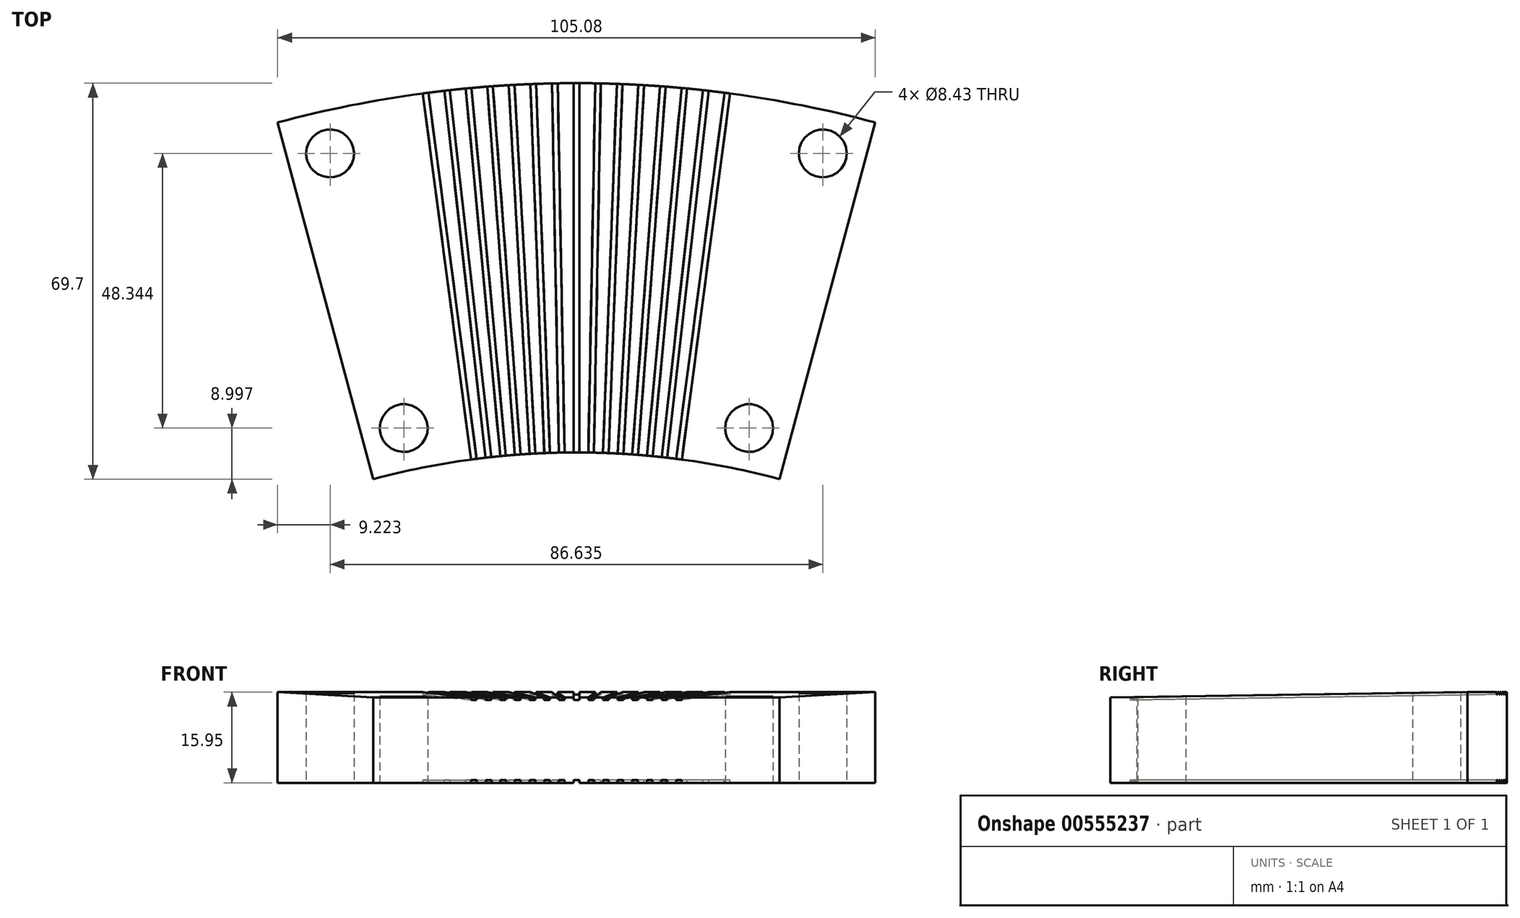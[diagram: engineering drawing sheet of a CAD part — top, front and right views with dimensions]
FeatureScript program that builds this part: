
annotation { "Feature Type Name" : "Feature", "Feature Type Description" : "" }
export const myFeature = defineFeature(function(context is Context, id is Id, definition is map)
    precondition{}
    {
        {
            var Q0;
            Q0=qCreatedBy(makeId("Right.planeOp"),FACE);
            var sketch = newSketch(context, id + "F0", { "sketchPlane" : qUnion([Q0])});
            skLineSegment(sketch, "E0", {"start": v(0, 0) * mm, "end": v(0, 15) * mm});
            skLineSegment(sketch, "E1", {"start": v(0, 15) * mm, "end": v(65, 15.95) * mm});
            skLineSegment(sketch, "E2", {"start": v(65, 15.95) * mm, "end": v(65, 0) * mm});
            skLineSegment(sketch, "E3", {"start": v(65, 0) * mm, "end": v(0, 0) * mm});
            skLineSegment(sketch, "E4", {"start": v(-138, 37.06) * mm, "end": v(-138, 5.42) * mm});
            skSolve(sketch);
        }
        {
            var Q0;
            Q0=makeQuery(id+"F0.imprint","IMPRINT",FACE,{"disambiguationData":[TD([[makeQuery(id+"F0.imprint","IMPRINT",EDGE,{"derivedFrom":sQuery(id+"F0.wireOp",EDGE,"E0")}),-1.0]])]});
            var Q1;
            Q1=sQuery(id+"F0.wireOp",EDGE,"E4");
            revolve(context, id + "F1", {"entities" : qUnion([Q0]), "axis" : qUnion([Q1]), "revolveType" : RevolveType.SYMMETRIC, "angle" : 30 * degree});
        }
        {
            var Q0;
            Q0=qCreatedBy(makeId("Top.planeOp"),FACE);
            var sketch = newSketch(context, id + "F2", { "sketchPlane" : qUnion([Q0])});
            skLineSegment(sketch, "E5", {"start": v(0, -138) * mm, "end": v(-26.5, 63.26) * mm});
            skLineSegment(sketch, "E6", {"start": v(0, -138) * mm, "end": v(26.5, 63.26) * mm});
            skLineSegment(sketch, "E7.1.0", {"start": v(0, -138) * mm, "end": v(-22.73, 63.72) * mm});
            skLineSegment(sketch, "E7.2.0", {"start": v(0, -138) * mm, "end": v(-18.95, 64.11) * mm});
            skLineSegment(sketch, "E7.3.0", {"start": v(0, -138) * mm, "end": v(-15.17, 64.43) * mm});
            skLineSegment(sketch, "E7.4.0", {"start": v(0, -138) * mm, "end": v(-11.38, 64.68) * mm});
            skLineSegment(sketch, "E7.5.0", {"start": v(0, -138) * mm, "end": v(-7.6, 64.86) * mm});
            skLineSegment(sketch, "E7.6.0", {"start": v(0, -138) * mm, "end": v(-3.8, 64.96) * mm});
            skLineSegment(sketch, "E7.7.0", {"start": v(0, -138) * mm, "end": v(0, 65) * mm});
            skLineSegment(sketch, "E7.8.0", {"start": v(0, -138) * mm, "end": v(3.8, 64.96) * mm});
            skLineSegment(sketch, "E7.9.0", {"start": v(0, -138) * mm, "end": v(7.6, 64.86) * mm});
            skLineSegment(sketch, "E7.10.0", {"start": v(0, -138) * mm, "end": v(11.38, 64.68) * mm});
            skLineSegment(sketch, "E7.11.0", {"start": v(0, -138) * mm, "end": v(15.17, 64.43) * mm});
            skLineSegment(sketch, "E7.12.0", {"start": v(0, -138) * mm, "end": v(18.95, 64.11) * mm});
            skLineSegment(sketch, "E7.13.0", {"start": v(0, -138) * mm, "end": v(22.73, 63.72) * mm});
            skPoint(sketch, "E7.center", {"position": v(0, -138) * mm});
            skLineSegment(sketch, "E7.anchor1", {"start": v(0, -138) * mm, "end": v(-26.5, 63.26) * mm, "construction": true});
            skLineSegment(sketch, "E7.anchor2", {"start": v(0, -138) * mm, "end": v(26.5, 63.26) * mm, "construction": true});
            skLineSegment(sketch, "E8.bottom", {"start": v(43.3, 187.13) * mm, "end": v(42.32, 187.26) * mm});
            skLineSegment(sketch, "E8.top", {"start": v(10.68, -60.73) * mm, "end": v(9.69, -60.6) * mm});
            skLineSegment(sketch, "E8.left", {"start": v(43.3, 187.13) * mm, "end": v(10.68, -60.73) * mm});
            skLineSegment(sketch, "E8.right", {"start": v(42.32, 187.26) * mm, "end": v(9.69, -60.6) * mm});
            skPoint(sketch, "E8.middle", {"position": v(26.5, 63.26) * mm});
            skLineSegment(sketch, "E9.bottom", {"start": v(37.22, 187.88) * mm, "end": v(36.23, 188) * mm});
            skLineSegment(sketch, "E9.top", {"start": v(9.23, -60.55) * mm, "end": v(8.24, -60.43) * mm});
            skLineSegment(sketch, "E9.left", {"start": v(37.22, 187.88) * mm, "end": v(9.23, -60.55) * mm});
            skLineSegment(sketch, "E9.right", {"start": v(36.23, 188) * mm, "end": v(8.24, -60.43) * mm});
            skPoint(sketch, "E9.middle", {"position": v(22.73, 63.72) * mm});
            skLineSegment(sketch, "E10.bottom", {"start": v(31.12, 188.52) * mm, "end": v(30.13, 188.61) * mm});
            skLineSegment(sketch, "E10.top", {"start": v(7.78, -60.39) * mm, "end": v(6.78, -60.3) * mm});
            skLineSegment(sketch, "E10.left", {"start": v(31.12, 188.52) * mm, "end": v(7.78, -60.39) * mm});
            skLineSegment(sketch, "E10.right", {"start": v(30.13, 188.61) * mm, "end": v(6.78, -60.3) * mm});
            skPoint(sketch, "E10.middle", {"position": v(18.95, 64.11) * mm});
            skLineSegment(sketch, "E11.bottom", {"start": v(25.01, 189.05) * mm, "end": v(24.01, 189.12) * mm});
            skLineSegment(sketch, "E11.top", {"start": v(6.33, -60.26) * mm, "end": v(5.33, -60.18) * mm});
            skLineSegment(sketch, "E11.left", {"start": v(25.01, 189.05) * mm, "end": v(6.33, -60.26) * mm});
            skLineSegment(sketch, "E11.right", {"start": v(24.01, 189.12) * mm, "end": v(5.33, -60.18) * mm});
            skPoint(sketch, "E11.middle", {"position": v(15.17, 64.43) * mm});
            skLineSegment(sketch, "E12.bottom", {"start": v(18.9, 189.46) * mm, "end": v(17.9, 189.51) * mm});
            skLineSegment(sketch, "E12.top", {"start": v(4.87, -60.15) * mm, "end": v(3.87, -60.1) * mm});
            skLineSegment(sketch, "E12.left", {"start": v(18.9, 189.46) * mm, "end": v(4.87, -60.15) * mm});
            skLineSegment(sketch, "E12.right", {"start": v(17.9, 189.51) * mm, "end": v(3.87, -60.1) * mm});
            skPoint(sketch, "E12.middle", {"position": v(11.38, 64.68) * mm});
            skLineSegment(sketch, "E13.bottom", {"start": v(6.63, 189.93) * mm, "end": v(5.63, 189.95) * mm});
            skLineSegment(sketch, "E13.top", {"start": v(1.96, -60.02) * mm, "end": v(0.96, -60) * mm});
            skLineSegment(sketch, "E13.left", {"start": v(6.63, 189.93) * mm, "end": v(1.96, -60.02) * mm});
            skLineSegment(sketch, "E13.right", {"start": v(5.63, 189.95) * mm, "end": v(0.96, -60) * mm});
            skPoint(sketch, "E13.middle", {"position": v(3.8, 64.96) * mm});
            skLineSegment(sketch, "E14.bottom", {"start": v(0.5, 190) * mm, "end": v(-0.5, 190) * mm});
            skLineSegment(sketch, "E14.top", {"start": v(0.5, -60) * mm, "end": v(-0.5, -60) * mm});
            skLineSegment(sketch, "E14.left", {"start": v(0.5, 190) * mm, "end": v(0.5, -60) * mm});
            skLineSegment(sketch, "E14.right", {"start": v(-0.5, 190) * mm, "end": v(-0.5, -60) * mm});
            skPoint(sketch, "E14.middle", {"position": v(0, 65) * mm});
            skLineSegment(sketch, "E15.bottom", {"start": v(12.76, 189.75) * mm, "end": v(11.76, 189.79) * mm});
            skLineSegment(sketch, "E15.top", {"start": v(3.42, -60.07) * mm, "end": v(2.42, -60.04) * mm});
            skLineSegment(sketch, "E15.left", {"start": v(12.76, 189.75) * mm, "end": v(3.42, -60.07) * mm});
            skLineSegment(sketch, "E15.right", {"start": v(11.76, 189.79) * mm, "end": v(2.42, -60.04) * mm});
            skPoint(sketch, "E15.middle", {"position": v(7.6, 64.86) * mm});
            skLineSegment(sketch, "E16.bottom", {"start": v(-5.63, 189.95) * mm, "end": v(-6.63, 189.93) * mm});
            skLineSegment(sketch, "E16.top", {"start": v(-0.96, -60) * mm, "end": v(-1.96, -60.02) * mm});
            skLineSegment(sketch, "E16.left", {"start": v(-5.63, 189.95) * mm, "end": v(-0.96, -60) * mm});
            skLineSegment(sketch, "E16.right", {"start": v(-6.63, 189.93) * mm, "end": v(-1.96, -60.02) * mm});
            skPoint(sketch, "E16.middle", {"position": v(-3.8, 64.96) * mm});
            skLineSegment(sketch, "E17.bottom", {"start": v(-30.13, 188.61) * mm, "end": v(-31.12, 188.52) * mm});
            skLineSegment(sketch, "E17.top", {"start": v(-6.78, -60.3) * mm, "end": v(-7.78, -60.39) * mm});
            skLineSegment(sketch, "E17.left", {"start": v(-30.13, 188.61) * mm, "end": v(-6.78, -60.3) * mm});
            skLineSegment(sketch, "E17.right", {"start": v(-31.12, 188.52) * mm, "end": v(-7.78, -60.39) * mm});
            skPoint(sketch, "E17.middle", {"position": v(-18.95, 64.11) * mm});
            skLineSegment(sketch, "E18.bottom", {"start": v(-36.23, 188) * mm, "end": v(-37.22, 187.88) * mm});
            skLineSegment(sketch, "E18.top", {"start": v(-8.24, -60.43) * mm, "end": v(-9.23, -60.55) * mm});
            skLineSegment(sketch, "E18.left", {"start": v(-36.23, 188) * mm, "end": v(-8.24, -60.43) * mm});
            skLineSegment(sketch, "E18.right", {"start": v(-37.22, 187.88) * mm, "end": v(-9.23, -60.55) * mm});
            skPoint(sketch, "E18.middle", {"position": v(-22.73, 63.72) * mm});
            skLineSegment(sketch, "E19.bottom", {"start": v(-42.32, 187.26) * mm, "end": v(-43.3, 187.13) * mm});
            skLineSegment(sketch, "E19.top", {"start": v(-9.69, -60.6) * mm, "end": v(-10.68, -60.73) * mm});
            skLineSegment(sketch, "E19.left", {"start": v(-42.32, 187.26) * mm, "end": v(-9.69, -60.6) * mm});
            skLineSegment(sketch, "E19.right", {"start": v(-43.3, 187.13) * mm, "end": v(-10.68, -60.73) * mm});
            skPoint(sketch, "E19.middle", {"position": v(-26.5, 63.26) * mm});
            skLineSegment(sketch, "E20.bottom", {"start": v(-24.01, 189.12) * mm, "end": v(-25.01, 189.05) * mm});
            skLineSegment(sketch, "E20.top", {"start": v(-5.33, -60.18) * mm, "end": v(-6.33, -60.26) * mm});
            skLineSegment(sketch, "E20.left", {"start": v(-24.01, 189.12) * mm, "end": v(-5.33, -60.18) * mm});
            skLineSegment(sketch, "E20.right", {"start": v(-25.01, 189.05) * mm, "end": v(-6.33, -60.26) * mm});
            skPoint(sketch, "E20.middle", {"position": v(-15.17, 64.43) * mm});
            skLineSegment(sketch, "E21.bottom", {"start": v(-17.9, 189.51) * mm, "end": v(-18.9, 189.46) * mm});
            skLineSegment(sketch, "E21.top", {"start": v(-3.87, -60.1) * mm, "end": v(-4.87, -60.15) * mm});
            skLineSegment(sketch, "E21.left", {"start": v(-17.9, 189.51) * mm, "end": v(-3.87, -60.1) * mm});
            skLineSegment(sketch, "E21.right", {"start": v(-18.9, 189.46) * mm, "end": v(-4.87, -60.15) * mm});
            skPoint(sketch, "E21.middle", {"position": v(-11.38, 64.68) * mm});
            skLineSegment(sketch, "E22.bottom", {"start": v(-11.76, 189.79) * mm, "end": v(-12.76, 189.75) * mm});
            skLineSegment(sketch, "E22.top", {"start": v(-2.42, -60.04) * mm, "end": v(-3.42, -60.07) * mm});
            skLineSegment(sketch, "E22.left", {"start": v(-11.76, 189.79) * mm, "end": v(-2.42, -60.04) * mm});
            skLineSegment(sketch, "E22.right", {"start": v(-12.76, 189.75) * mm, "end": v(-3.42, -60.07) * mm});
            skPoint(sketch, "E22.middle", {"position": v(-7.6, 64.86) * mm});
            skSolve(sketch);
        }
        {
            var Q0;
            Q0 = qSketchRegion(id + "F2", true);
            extrude(context, id + "F3", {"entities" : qUnion([Q0]), "operationType" : NewBodyOperationType.REMOVE, "depth" : .5 * mm, "offsetDistance" : 25 * mm});
        }
        {
            var Q0;
            Q0=makeQuery(id+"F1.opRevolve","CAP_VERTEX",VERTEX,{"disambiguationData":[OSD([sQuery(id+"F0.wireOp",EDGE,"E1"),sQuery(id+"F0.wireOp",EDGE,"E2")])],"isStart":true});
            var Q1;
            Q1=makeQuery(id+"F1.opRevolve","CAP_VERTEX",VERTEX,{"disambiguationData":[OSD([sQuery(id+"F0.wireOp",EDGE,"E1"),sQuery(id+"F0.wireOp",EDGE,"E2")])],"isStart":false});
            var Q2;
            Q2=makeQuery(id+"F1.opRevolve","CAP_VERTEX",VERTEX,{"disambiguationData":[OSD([sQuery(id+"F0.wireOp",EDGE,"E0"),sQuery(id+"F0.wireOp",EDGE,"E1")])],"isStart":false});
            cPlane(context, id + "F4", {"entities" : qUnion([Q0, Q1, Q2]), "cplaneType" : CPlaneType.THREE_POINT, "offset" : 25 * mm, "width" : 150 * mm, "height" : 150 * mm});
        }
        {
            var Q0;
            Q0=qCreatedBy(id+"F4.planeOp",FACE);
            var sketch = newSketch(context, id + "F5", { "sketchPlane" : qUnion([Q0])});
            skLineSegment(sketch, "E23", {"start": v(0, -137.98) * mm, "end": v(-26.5, 63.28) * mm});
            skLineSegment(sketch, "E24", {"start": v(0, -137.98) * mm, "end": v(26.5, 63.28) * mm});
            skLineSegment(sketch, "E25.1.0", {"start": v(0, -137.98) * mm, "end": v(-22.73, 63.74) * mm});
            skLineSegment(sketch, "E25.2.0", {"start": v(0, -137.98) * mm, "end": v(-18.95, 64.13) * mm});
            skLineSegment(sketch, "E25.3.0", {"start": v(0, -137.98) * mm, "end": v(-15.17, 64.45) * mm});
            skLineSegment(sketch, "E25.4.0", {"start": v(0, -137.98) * mm, "end": v(-11.38, 64.7) * mm});
            skLineSegment(sketch, "E25.5.0", {"start": v(0, -137.98) * mm, "end": v(-7.6, 64.87) * mm});
            skLineSegment(sketch, "E25.6.0", {"start": v(0, -137.98) * mm, "end": v(-3.8, 64.98) * mm});
            skLineSegment(sketch, "E25.7.0", {"start": v(0, -137.98) * mm, "end": v(0, 65.02) * mm});
            skLineSegment(sketch, "E25.8.0", {"start": v(0, -137.98) * mm, "end": v(3.8, 64.98) * mm});
            skLineSegment(sketch, "E25.9.0", {"start": v(0, -137.98) * mm, "end": v(7.6, 64.87) * mm});
            skLineSegment(sketch, "E25.10.0", {"start": v(0, -137.98) * mm, "end": v(11.38, 64.7) * mm});
            skLineSegment(sketch, "E25.11.0", {"start": v(0, -137.98) * mm, "end": v(15.17, 64.45) * mm});
            skLineSegment(sketch, "E25.12.0", {"start": v(0, -137.98) * mm, "end": v(18.95, 64.13) * mm});
            skLineSegment(sketch, "E25.13.0", {"start": v(0, -137.98) * mm, "end": v(22.73, 63.74) * mm});
            skPoint(sketch, "E25.center", {"position": v(0, -137.98) * mm});
            skLineSegment(sketch, "E25.anchor1", {"start": v(0, -137.98) * mm, "end": v(-26.5, 63.28) * mm, "construction": true});
            skLineSegment(sketch, "E25.anchor2", {"start": v(0, -137.98) * mm, "end": v(26.5, 63.28) * mm, "construction": true});
            skLineSegment(sketch, "E26.bottom", {"start": v(43.3, 187.14) * mm, "end": v(42.32, 187.27) * mm});
            skLineSegment(sketch, "E26.top", {"start": v(10.68, -60.72) * mm, "end": v(9.69, -60.59) * mm});
            skLineSegment(sketch, "E26.left", {"start": v(43.3, 187.14) * mm, "end": v(10.68, -60.72) * mm});
            skLineSegment(sketch, "E26.right", {"start": v(42.32, 187.27) * mm, "end": v(9.69, -60.59) * mm});
            skPoint(sketch, "E26.middle", {"position": v(26.5, 63.28) * mm});
            skLineSegment(sketch, "E27.bottom", {"start": v(37.22, 187.9) * mm, "end": v(36.23, 188) * mm});
            skLineSegment(sketch, "E27.top", {"start": v(9.23, -60.53) * mm, "end": v(8.24, -60.42) * mm});
            skLineSegment(sketch, "E27.left", {"start": v(37.22, 187.9) * mm, "end": v(9.23, -60.53) * mm});
            skLineSegment(sketch, "E27.right", {"start": v(36.23, 188) * mm, "end": v(8.24, -60.42) * mm});
            skPoint(sketch, "E27.middle", {"position": v(22.73, 63.74) * mm});
            skLineSegment(sketch, "E28.bottom", {"start": v(31.12, 188.54) * mm, "end": v(30.13, 188.63) * mm});
            skLineSegment(sketch, "E28.top", {"start": v(7.78, -60.37) * mm, "end": v(6.78, -60.28) * mm});
            skLineSegment(sketch, "E28.left", {"start": v(31.12, 188.54) * mm, "end": v(7.78, -60.37) * mm});
            skLineSegment(sketch, "E28.right", {"start": v(30.13, 188.63) * mm, "end": v(6.78, -60.28) * mm});
            skPoint(sketch, "E28.middle", {"position": v(18.95, 64.13) * mm});
            skLineSegment(sketch, "E29.bottom", {"start": v(25.01, 189.06) * mm, "end": v(24.01, 189.14) * mm});
            skLineSegment(sketch, "E29.top", {"start": v(6.33, -60.24) * mm, "end": v(5.33, -60.16) * mm});
            skLineSegment(sketch, "E29.left", {"start": v(25.01, 189.06) * mm, "end": v(6.33, -60.24) * mm});
            skLineSegment(sketch, "E29.right", {"start": v(24.01, 189.14) * mm, "end": v(5.33, -60.16) * mm});
            skPoint(sketch, "E29.middle", {"position": v(15.17, 64.45) * mm});
            skLineSegment(sketch, "E30.bottom", {"start": v(18.9, 189.47) * mm, "end": v(17.9, 189.53) * mm});
            skLineSegment(sketch, "E30.top", {"start": v(4.87, -60.13) * mm, "end": v(3.87, -60.08) * mm});
            skLineSegment(sketch, "E30.left", {"start": v(18.9, 189.47) * mm, "end": v(4.87, -60.13) * mm});
            skLineSegment(sketch, "E30.right", {"start": v(17.9, 189.53) * mm, "end": v(3.87, -60.08) * mm});
            skPoint(sketch, "E30.middle", {"position": v(11.38, 64.7) * mm});
            skLineSegment(sketch, "E31.bottom", {"start": v(6.63, 189.95) * mm, "end": v(5.63, 189.97) * mm});
            skLineSegment(sketch, "E31.top", {"start": v(1.96, -60) * mm, "end": v(0.96, -59.99) * mm});
            skLineSegment(sketch, "E31.left", {"start": v(6.63, 189.95) * mm, "end": v(1.96, -60) * mm});
            skLineSegment(sketch, "E31.right", {"start": v(5.63, 189.97) * mm, "end": v(0.96, -59.99) * mm});
            skPoint(sketch, "E31.middle", {"position": v(3.8, 64.98) * mm});
            skLineSegment(sketch, "E32.bottom", {"start": v(0.5, 190.02) * mm, "end": v(-0.5, 190.02) * mm});
            skLineSegment(sketch, "E32.top", {"start": v(0.5, -59.98) * mm, "end": v(-0.5, -59.98) * mm});
            skLineSegment(sketch, "E32.left", {"start": v(0.5, 190.02) * mm, "end": v(0.5, -59.98) * mm});
            skLineSegment(sketch, "E32.right", {"start": v(-0.5, 190.02) * mm, "end": v(-0.5, -59.98) * mm});
            skPoint(sketch, "E32.middle", {"position": v(0, 65.02) * mm});
            skLineSegment(sketch, "E33.bottom", {"start": v(12.76, 189.77) * mm, "end": v(11.76, 189.8) * mm});
            skLineSegment(sketch, "E33.top", {"start": v(3.42, -60.06) * mm, "end": v(2.42, -60.02) * mm});
            skLineSegment(sketch, "E33.left", {"start": v(12.76, 189.77) * mm, "end": v(3.42, -60.06) * mm});
            skLineSegment(sketch, "E33.right", {"start": v(11.76, 189.8) * mm, "end": v(2.42, -60.02) * mm});
            skPoint(sketch, "E33.middle", {"position": v(7.6, 64.87) * mm});
            skLineSegment(sketch, "E34.bottom", {"start": v(-5.63, 189.97) * mm, "end": v(-6.63, 189.95) * mm});
            skLineSegment(sketch, "E34.top", {"start": v(-0.96, -59.99) * mm, "end": v(-1.96, -60) * mm});
            skLineSegment(sketch, "E34.left", {"start": v(-5.63, 189.97) * mm, "end": v(-0.96, -59.99) * mm});
            skLineSegment(sketch, "E34.right", {"start": v(-6.63, 189.95) * mm, "end": v(-1.96, -60) * mm});
            skPoint(sketch, "E34.middle", {"position": v(-3.8, 64.98) * mm});
            skLineSegment(sketch, "E35.bottom", {"start": v(-30.13, 188.63) * mm, "end": v(-31.12, 188.54) * mm});
            skLineSegment(sketch, "E35.top", {"start": v(-6.78, -60.28) * mm, "end": v(-7.78, -60.37) * mm});
            skLineSegment(sketch, "E35.left", {"start": v(-30.13, 188.63) * mm, "end": v(-6.78, -60.28) * mm});
            skLineSegment(sketch, "E35.right", {"start": v(-31.12, 188.54) * mm, "end": v(-7.78, -60.37) * mm});
            skPoint(sketch, "E35.middle", {"position": v(-18.95, 64.13) * mm});
            skLineSegment(sketch, "E36.bottom", {"start": v(-36.23, 188) * mm, "end": v(-37.22, 187.9) * mm});
            skLineSegment(sketch, "E36.top", {"start": v(-8.24, -60.42) * mm, "end": v(-9.23, -60.53) * mm});
            skLineSegment(sketch, "E36.left", {"start": v(-36.23, 188) * mm, "end": v(-8.24, -60.42) * mm});
            skLineSegment(sketch, "E36.right", {"start": v(-37.22, 187.9) * mm, "end": v(-9.23, -60.53) * mm});
            skPoint(sketch, "E36.middle", {"position": v(-22.73, 63.74) * mm});
            skLineSegment(sketch, "E37.bottom", {"start": v(-42.32, 187.27) * mm, "end": v(-43.3, 187.14) * mm});
            skLineSegment(sketch, "E37.top", {"start": v(-9.69, -60.59) * mm, "end": v(-10.68, -60.72) * mm});
            skLineSegment(sketch, "E37.left", {"start": v(-42.32, 187.27) * mm, "end": v(-9.69, -60.59) * mm});
            skLineSegment(sketch, "E37.right", {"start": v(-43.3, 187.14) * mm, "end": v(-10.68, -60.72) * mm});
            skPoint(sketch, "E37.middle", {"position": v(-26.5, 63.28) * mm});
            skLineSegment(sketch, "E38.bottom", {"start": v(-24.01, 189.14) * mm, "end": v(-25.01, 189.06) * mm});
            skLineSegment(sketch, "E38.top", {"start": v(-5.33, -60.16) * mm, "end": v(-6.33, -60.24) * mm});
            skLineSegment(sketch, "E38.left", {"start": v(-24.01, 189.14) * mm, "end": v(-5.33, -60.16) * mm});
            skLineSegment(sketch, "E38.right", {"start": v(-25.01, 189.06) * mm, "end": v(-6.33, -60.24) * mm});
            skPoint(sketch, "E38.middle", {"position": v(-15.17, 64.45) * mm});
            skLineSegment(sketch, "E39.bottom", {"start": v(-17.9, 189.53) * mm, "end": v(-18.9, 189.47) * mm});
            skLineSegment(sketch, "E39.top", {"start": v(-3.87, -60.08) * mm, "end": v(-4.87, -60.13) * mm});
            skLineSegment(sketch, "E39.left", {"start": v(-17.9, 189.53) * mm, "end": v(-3.87, -60.08) * mm});
            skLineSegment(sketch, "E39.right", {"start": v(-18.9, 189.47) * mm, "end": v(-4.87, -60.13) * mm});
            skPoint(sketch, "E39.middle", {"position": v(-11.38, 64.7) * mm});
            skLineSegment(sketch, "E40.bottom", {"start": v(-11.76, 189.8) * mm, "end": v(-12.76, 189.77) * mm});
            skLineSegment(sketch, "E40.top", {"start": v(-2.42, -60.02) * mm, "end": v(-3.42, -60.06) * mm});
            skLineSegment(sketch, "E40.left", {"start": v(-11.76, 189.8) * mm, "end": v(-2.42, -60.02) * mm});
            skLineSegment(sketch, "E40.right", {"start": v(-12.76, 189.77) * mm, "end": v(-3.42, -60.06) * mm});
            skPoint(sketch, "E40.middle", {"position": v(-7.6, 64.87) * mm});
            skSolve(sketch);
        }
        {
            var Q0;
            Q0 = qSketchRegion(id + "F5", true);
            extrude(context, id + "F6", {"entities" : qUnion([Q0]), "operationType" : NewBodyOperationType.REMOVE, "oppositeDirection" : true, "depth" : .5 * mm, "offsetDistance" : 25 * mm});
        }
        {
            var Q0;
            Q0=qCreatedBy(makeId("Top.planeOp"),FACE);
            var sketch = newSketch(context, id + "F7", { "sketchPlane" : qUnion([Q0])});
            skCircle(sketch, "E41", {"center": v(-30.36, 4.3) * mm, "radius": 7.5 * mm});
            skCircle(sketch, "E42", {"center": v(30.36, 4.3) * mm, "radius": 7.5 * mm});
            skCircle(sketch, "E43", {"center": v(43.32, 52.64) * mm, "radius": 7.5 * mm});
            skCircle(sketch, "E44", {"center": v(-43.32, 52.64) * mm, "radius": 7.5 * mm});
            skSolve(sketch);
        }
        {
            var Q0;
            Q0=sQuery(id+"F7.wireOp",VERTEX,"E41.center");
            var Q1;
            Q1=sQuery(id+"F7.wireOp",VERTEX,"E42.center");
            var Q2;
            Q2=sQuery(id+"F7.wireOp",VERTEX,"E43.center");
            var Q3;
            Q3=sQuery(id+"F7.wireOp",VERTEX,"E44.center");
            var Q4;
            Q4=makeQuery(id+"F1.opRevolve","SWEPT_BODY",BODY,{"disambiguationData":[OSD([sQuery(id+"F0.wireOp",EDGE,"E0"),sQuery(id+"F0.wireOp",EDGE,"E1"),sQuery(id+"F0.wireOp",EDGE,"E2"),sQuery(id+"F0.wireOp",EDGE,"E3")])]});
            hole(context, id + "F8", {"style" : HoleStyle.SIMPLE, "endStyle" : HoleEndStyle.THROUGH, "oppositeDirection" : true, "standardTappedOrClearance" : lookupTablePath({ "standard" : "ANSI", "fit" : "Normal (ASME)", "size" : "5/16", "type" : "Clearance" }), "standardBlindInLast" : lookupTablePath({ "fit" : "Free", "standard" : "ANSI", "size" : "5/16", "type" : "Clearance" }), "holeDiameter" : 8.43 * mm, "isTappedThrough" : true, "tappedDepth" : 12 * mm, "tapClearance" : 3, "locations" : qUnion([Q0, Q1, Q2, Q3]), "scope" : qUnion([Q4])});
        }
    });
